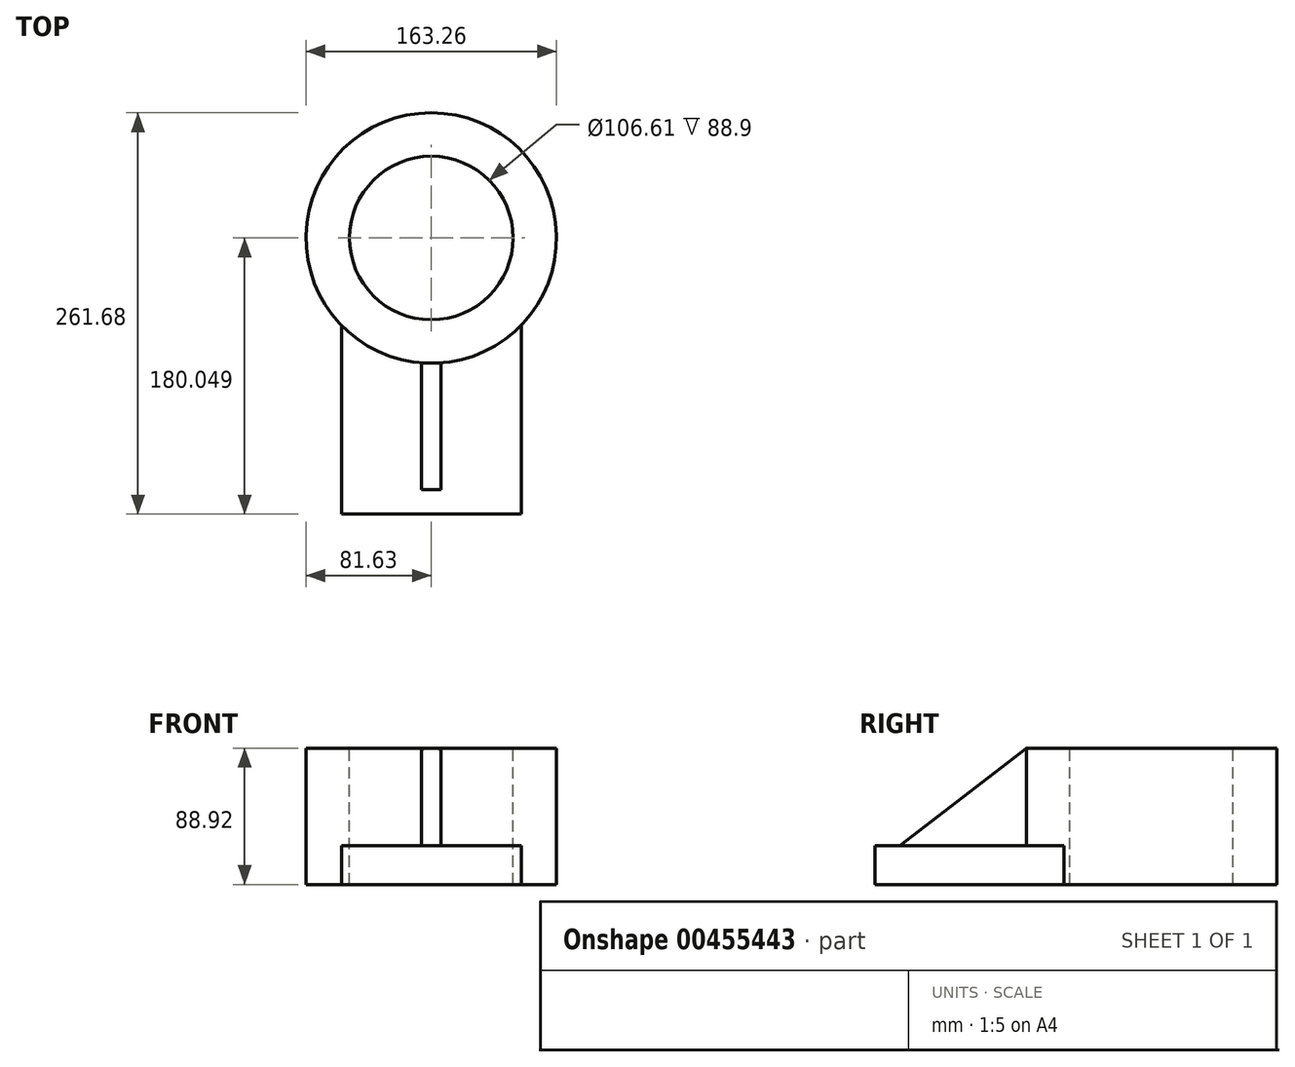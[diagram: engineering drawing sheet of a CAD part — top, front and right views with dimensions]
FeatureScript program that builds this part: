
annotation { "Feature Type Name" : "Feature", "Feature Type Description" : "" }
export const myFeature = defineFeature(function(context is Context, id is Id, definition is map)
    precondition{}
    {
        {
            var Q0;
            Q0=qCreatedBy(makeId("Top.planeOp"),FACE);
            var sketch = newSketch(context, id + "F0", { "sketchPlane" : qUnion([Q0])});
            skLineSegment(sketch, "E0.bottom", {"start": v(58.57, -63.85) * mm, "end": v(-58.57, -63.85) * mm});
            skLineSegment(sketch, "E0.top", {"start": v(58.57, 63.85) * mm, "end": v(-58.57, 63.85) * mm});
            skLineSegment(sketch, "E0.left", {"start": v(58.57, -63.85) * mm, "end": v(58.57, 63.85) * mm});
            skLineSegment(sketch, "E0.right", {"start": v(-58.57, -63.85) * mm, "end": v(-58.57, 63.85) * mm});
            skCircle(sketch, "E1", {"center": v(0, 116.2) * mm, "radius": 81.63 * mm});
            skCircle(sketch, "E2", {"center": v(0, 116.2) * mm, "radius": 53.3 * mm});
            skSolve(sketch);
        }
        {
            var Q0;
            Q0 = qSketchRegion(id + "F0", true);
            var Q1;
            Q1=makeQuery(id+"F0.imprint","IMPRINT",FACE,{"disambiguationData":[TD([[makeQuery(id+"F0.imprint","IMPRINT",EDGE,{"derivedFrom":sQuery(id+"F0.wireOp",EDGE,"g6fTBQg7-6DWr-ZRkt-GHdy-fIqn2KDRyn2F.bottom")}),-1.0]])]});
            var Q2;
            {var subQ0=sQuery(id+"F0.wireOp",EDGE,"g6fTBQg7-6DWr-ZRkt-GHdy-fIqn2KDRyn2F.top");var subQ1=sQuery(id+"F0.wireOp",EDGE,"E1");var subQ3=makeQuery(id+"F0.imprint","INTERSECT",VERTEX,{"derivedFrom":[subQ1,subQ0]});Q2=makeQuery(id+"F0.imprint","IMPRINT",FACE,{"disambiguationData":[TD([[makeQuery(id+"F0.imprint","IMPRINT",EDGE,{"disambiguationData":[TD([[subQ3,1.0]])],"derivedFrom":subQ1}),1.0]])]});}
            extrude(context, id + "F1", {"entities" : qUnion([Q0, Q1, Q2]), "oppositeDirection" : true, "depth" : 25.4 * mm});
        }
        {
            var Q0;
            {var subQ1=sQuery(id+"F0.wireOp",EDGE,"E0.top");var subQ5=sQuery(id+"F0.wireOp",EDGE,"E0.left");var subQ6=makeQuery(id+"F0.imprint","INTERSECT",VERTEX,{"derivedFrom":[subQ1,subQ5]});Q0=makeQuery(id+"F0.imprint","IMPRINT",FACE,{"disambiguationData":[TD([[makeQuery(id+"F0.imprint","IMPRINT",EDGE,{"disambiguationData":[TD([[subQ6,-1.0]])],"derivedFrom":subQ1}),-1.0]])]});}
            var Q1;
            {var subQ1=sQuery(id+"F0.wireOp",EDGE,"E0.top");var subQ5=sQuery(id+"F0.wireOp",EDGE,"E0.left");var subQ6=makeQuery(id+"F0.imprint","INTERSECT",VERTEX,{"derivedFrom":[subQ1,subQ5]});Q1=makeQuery(id+"F0.imprint","IMPRINT",FACE,{"disambiguationData":[TD([[makeQuery(id+"F0.imprint","IMPRINT",EDGE,{"disambiguationData":[TD([[subQ6,-1.0]])],"derivedFrom":subQ1}),1.0]])]});}
            var Q2;
            {var subQ0=sQuery(id+"F0.wireOp",EDGE,"g6fTBQg7-6DWr-ZRkt-GHdy-fIqn2KDRyn2F.top");var subQ1=sQuery(id+"F0.wireOp",EDGE,"E1");var subQ3=makeQuery(id+"F0.imprint","INTERSECT",VERTEX,{"derivedFrom":[subQ1,subQ0]});Q2=makeQuery(id+"F0.imprint","IMPRINT",FACE,{"disambiguationData":[TD([[makeQuery(id+"F0.imprint","IMPRINT",EDGE,{"disambiguationData":[TD([[subQ3,1.0]])],"derivedFrom":subQ1}),1.0]])]});}
            extrude(context, id + "F2", {"entities" : qUnion([Q0, Q1, Q2]), "operationType" : NewBodyOperationType.ADD, "depth" : 63.5 * mm});
        }
        {
            var Q0;
            Q0=qCreatedBy(makeId("Right.planeOp"),FACE);
            var sketch = newSketch(context, id + "F3", { "sketchPlane" : qUnion([Q0])});
            skLineSegment(sketch, "E3", {"start": v(34.65, 63.52) * mm, "end": v(-47.82, 0) * mm});
            skLineSegment(sketch, "E4", {"start": v(-47.82, 0) * mm, "end": v(39.58, 0) * mm});
            skLineSegment(sketch, "E5", {"start": v(39.58, 0) * mm, "end": v(34.65, 63.52) * mm});
            skSolve(sketch);
        }
        {
            var Q0;
            Q0=makeQuery(id+"F3.imprint","IMPRINT",FACE,{"disambiguationData":[TD([[makeQuery(id+"F3.imprint","IMPRINT",EDGE,{"derivedFrom":sQuery(id+"F3.wireOp",EDGE,"E3")}),1.0]])]});
            extrude(context, id + "F4", {"entities" : qUnion([Q0]), "operationType" : NewBodyOperationType.ADD, "depth" : 6.35 * mm, "hasSecondDirection" : true, "secondDirectionOppositeDirection" : true, "secondDirectionDepth" : 6.35 * mm});
        }
    });
